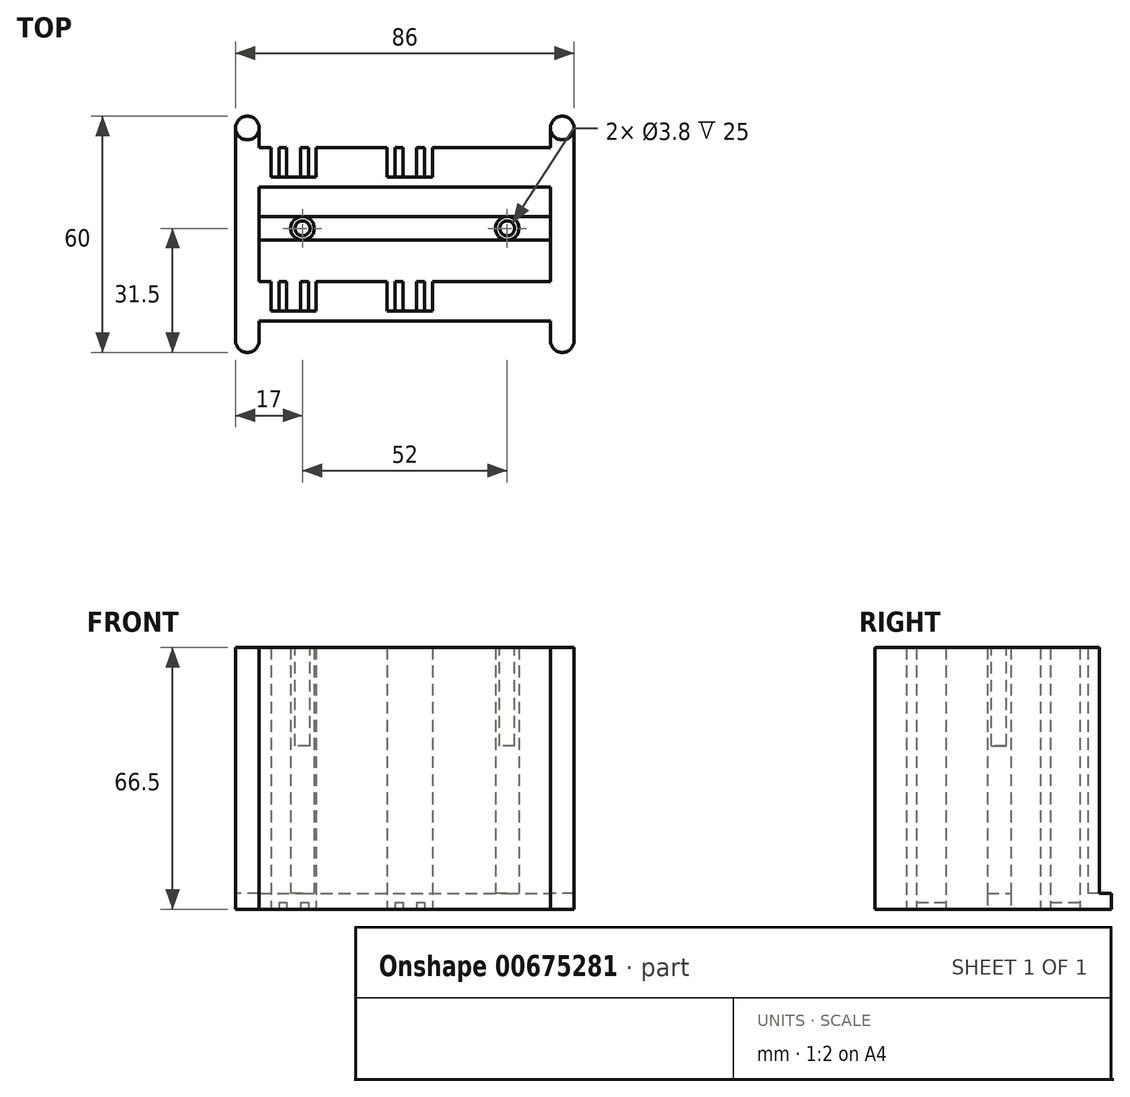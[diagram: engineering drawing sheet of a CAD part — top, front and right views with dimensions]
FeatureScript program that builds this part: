
annotation { "Feature Type Name" : "Feature", "Feature Type Description" : "" }
export const myFeature = defineFeature(function(context is Context, id is Id, definition is map)
    precondition{}
    {
        {
            var Q0;
            Q0=qCreatedBy(makeId("Top.planeOp"),FACE);
            var sketch = newSketch(context, id + "F0", { "sketchPlane" : qUnion([Q0])});
            skLineSegment(sketch, "E0", {"start": v(80, 0) * mm, "end": v(80, -39) * mm});
            skLineSegment(sketch, "E1", {"start": v(86, -39) * mm, "end": v(86, 15) * mm});
            skLineSegment(sketch, "E2", {"start": v(80, 15) * mm, "end": v(80, 10) * mm});
            skLineSegment(sketch, "E3", {"start": v(80, 10) * mm, "end": v(50, 10) * mm});
            skLineSegment(sketch, "E4", {"start": v(50, 10) * mm, "end": v(50, 2.5) * mm});
            skLineSegment(sketch, "E5", {"start": v(50, 2.5) * mm, "end": v(38.5, 2.5) * mm});
            skLineSegment(sketch, "E6", {"start": v(38.5, 2.5) * mm, "end": v(38.5, 10) * mm});
            skLineSegment(sketch, "E7", {"start": v(38.5, 10) * mm, "end": v(20.5, 10) * mm});
            skLineSegment(sketch, "E8", {"start": v(20.5, 10) * mm, "end": v(20.5, 2.5) * mm});
            skLineSegment(sketch, "E9", {"start": v(20.5, 2.5) * mm, "end": v(9, 2.5) * mm});
            skLineSegment(sketch, "E10", {"start": v(9, 2.5) * mm, "end": v(9, 10) * mm});
            skLineSegment(sketch, "E11", {"start": v(9, 10) * mm, "end": v(6, 10) * mm});
            skLineSegment(sketch, "E12", {"start": v(6, 10) * mm, "end": v(6, 15) * mm});
            skLineSegment(sketch, "E13", {"start": v(0, 15) * mm, "end": v(0, -39) * mm});
            skLineSegment(sketch, "E14", {"start": v(6, -39) * mm, "end": v(6, 0) * mm});
            skArc(sketch, "E15", {"start": v(0, 15) * mm, "mid": v(3, 18) * mm, "end": v(6, 15) * mm});
            skArc(sketch, "E16", {"start": v(6, -39) * mm, "mid": v(3, -42) * mm, "end": v(0, -39) * mm});
            skArc(sketch, "E17", {"start": v(86, -39) * mm, "mid": v(83, -42) * mm, "end": v(80, -39) * mm});
            skArc(sketch, "E18", {"start": v(80, 15) * mm, "mid": v(83, 18) * mm, "end": v(86, 15) * mm});
            skLineSegment(sketch, "E19", {"start": v(6, 0) * mm, "end": v(80, 0) * mm});
            skLineSegment(sketch, "E20.0.1.0", {"start": v(9, -24) * mm, "end": v(6, -24) * mm});
            skLineSegment(sketch, "E20.0.1.1", {"start": v(9, -31.5) * mm, "end": v(9, -24) * mm});
            skLineSegment(sketch, "E20.0.1.2", {"start": v(20.5, -31.5) * mm, "end": v(9, -31.5) * mm});
            skLineSegment(sketch, "E20.0.1.3", {"start": v(6, -34) * mm, "end": v(80, -34) * mm});
            skLineSegment(sketch, "E20.0.1.4", {"start": v(38.5, -24) * mm, "end": v(20.5, -24) * mm});
            skLineSegment(sketch, "E20.0.1.5", {"start": v(20.5, -24) * mm, "end": v(20.5, -31.5) * mm});
            skLineSegment(sketch, "E20.0.1.6", {"start": v(38.5, -31.5) * mm, "end": v(38.5, -24) * mm});
            skLineSegment(sketch, "E20.0.1.7", {"start": v(50, -31.5) * mm, "end": v(38.5, -31.5) * mm});
            skLineSegment(sketch, "E20.0.1.8", {"start": v(50, -24) * mm, "end": v(50, -31.5) * mm});
            skLineSegment(sketch, "E20.0.1.9", {"start": v(80, -24) * mm, "end": v(50, -24) * mm});
            skLineSegment(sketch, "E20.direction1", {"start": v(6, 10) * mm, "end": v(25.1, 10) * mm, "construction": true});
            skLineSegment(sketch, "E20.direction2", {"start": v(6, 10) * mm, "end": v(6, -24) * mm, "construction": true});
            skSolve(sketch);
        }
        {
            var Q0;
            Q0=makeQuery(id+"F0.imprint","IMPRINT",FACE,{"disambiguationData":[TD([[makeQuery(id+"F0.imprint","IMPRINT",EDGE,{"derivedFrom":sQuery(id+"F0.wireOp",EDGE,"E0")}),1.0]])]});
            var Q1;
            {var subQ3=sQuery(id+"F0.wireOp",EDGE,"E20.0.1.0");Q1=makeQuery(id+"F0.imprint","IMPRINT",FACE,{"disambiguationData":[TD([[makeQuery(id+"F0.imprint","IMPRINT",EDGE,{"derivedFrom":subQ3}),1.0]])]});}
            extrude(context, id + "F1", {"entities" : qUnion([Q0, Q1]), "depth" : 4 * mm, "offsetDistance" : 25 * mm});
        }
        {
            var Q0;
            Q0=qCreatedBy(makeId("Top.planeOp"),FACE);
            var sketch = newSketch(context, id + "F2", { "sketchPlane" : qUnion([Q0])});
            skLineSegment(sketch, "E21.bottom", {"start": v(11, 2.5) * mm, "end": v(13, 2.5) * mm});
            skLineSegment(sketch, "E21.top", {"start": v(11, 10) * mm, "end": v(13, 10) * mm});
            skLineSegment(sketch, "E21.left", {"start": v(11, 2.5) * mm, "end": v(11, 10) * mm});
            skLineSegment(sketch, "E21.right", {"start": v(13, 2.5) * mm, "end": v(13, 10) * mm});
            skLineSegment(sketch, "E22.bottom", {"start": v(16.5, 2.5) * mm, "end": v(18.5, 2.5) * mm});
            skLineSegment(sketch, "E22.top", {"start": v(16.5, 10) * mm, "end": v(18.5, 10) * mm});
            skLineSegment(sketch, "E22.left", {"start": v(16.5, 2.5) * mm, "end": v(16.5, 10) * mm});
            skLineSegment(sketch, "E22.right", {"start": v(18.5, 2.5) * mm, "end": v(18.5, 10) * mm});
            skLineSegment(sketch, "E23.bottom", {"start": v(40.5, 2.5) * mm, "end": v(42.5, 2.5) * mm});
            skLineSegment(sketch, "E23.top", {"start": v(40.5, 10) * mm, "end": v(42.5, 10) * mm});
            skLineSegment(sketch, "E23.left", {"start": v(40.5, 2.5) * mm, "end": v(40.5, 10) * mm});
            skLineSegment(sketch, "E23.right", {"start": v(42.5, 2.5) * mm, "end": v(42.5, 10) * mm});
            skLineSegment(sketch, "E24.bottom", {"start": v(46, 2.5) * mm, "end": v(48, 2.5) * mm});
            skLineSegment(sketch, "E24.top", {"start": v(46, 10) * mm, "end": v(48, 10) * mm});
            skLineSegment(sketch, "E24.left", {"start": v(46, 2.5) * mm, "end": v(46, 10) * mm});
            skLineSegment(sketch, "E24.right", {"start": v(48, 2.5) * mm, "end": v(48, 10) * mm});
            skLineSegment(sketch, "E25.0.1.0", {"start": v(46, -31.5) * mm, "end": v(46, -24) * mm});
            skLineSegment(sketch, "E25.0.1.1", {"start": v(48, -31.5) * mm, "end": v(48, -24) * mm});
            skLineSegment(sketch, "E25.0.1.2", {"start": v(11, -31.5) * mm, "end": v(11, -24) * mm});
            skLineSegment(sketch, "E25.0.1.3", {"start": v(13, -31.5) * mm, "end": v(13, -24) * mm});
            skLineSegment(sketch, "E25.0.1.4", {"start": v(16.5, -31.5) * mm, "end": v(16.5, -24) * mm});
            skLineSegment(sketch, "E25.0.1.5", {"start": v(18.5, -31.5) * mm, "end": v(18.5, -24) * mm});
            skLineSegment(sketch, "E25.0.1.6", {"start": v(40.5, -31.5) * mm, "end": v(40.5, -24) * mm});
            skLineSegment(sketch, "E25.0.1.7", {"start": v(42.5, -31.5) * mm, "end": v(42.5, -24) * mm});
            skLineSegment(sketch, "E25.0.1.8", {"start": v(46, -24) * mm, "end": v(48, -24) * mm});
            skLineSegment(sketch, "E25.0.1.9", {"start": v(11, -31.5) * mm, "end": v(13, -31.5) * mm});
            skLineSegment(sketch, "E25.0.1.10", {"start": v(11, -24) * mm, "end": v(13, -24) * mm});
            skLineSegment(sketch, "E25.0.1.11", {"start": v(16.5, -31.5) * mm, "end": v(18.5, -31.5) * mm});
            skLineSegment(sketch, "E25.0.1.12", {"start": v(16.5, -24) * mm, "end": v(18.5, -24) * mm});
            skLineSegment(sketch, "E25.0.1.13", {"start": v(40.5, -31.5) * mm, "end": v(42.5, -31.5) * mm});
            skLineSegment(sketch, "E25.0.1.14", {"start": v(40.5, -24) * mm, "end": v(42.5, -24) * mm});
            skLineSegment(sketch, "E25.0.1.15", {"start": v(46, -31.5) * mm, "end": v(48, -31.5) * mm});
            skLineSegment(sketch, "E25.direction1", {"start": v(11, 2.5) * mm, "end": v(36, 2.5) * mm, "construction": true});
            skLineSegment(sketch, "E25.direction2", {"start": v(11, 2.5) * mm, "end": v(11, -31.5) * mm, "construction": true});
            skSolve(sketch);
        }
        {
            var Q0;
            Q0=makeQuery(id+"F2.imprint","IMPRINT",FACE,{"disambiguationData":[TD([[makeQuery(id+"F2.imprint","IMPRINT",EDGE,{"derivedFrom":sQuery(id+"F2.wireOp",EDGE,"E21.bottom")}),1.0]])]});
            var Q1;
            Q1=makeQuery(id+"F2.imprint","IMPRINT",FACE,{"disambiguationData":[TD([[makeQuery(id+"F2.imprint","IMPRINT",EDGE,{"derivedFrom":sQuery(id+"F2.wireOp",EDGE,"E22.bottom")}),1.0]])]});
            var Q2;
            Q2=makeQuery(id+"F2.imprint","IMPRINT",FACE,{"disambiguationData":[TD([[makeQuery(id+"F2.imprint","IMPRINT",EDGE,{"derivedFrom":sQuery(id+"F2.wireOp",EDGE,"E23.bottom")}),1.0]])]});
            var Q3;
            Q3=makeQuery(id+"F2.imprint","IMPRINT",FACE,{"disambiguationData":[TD([[makeQuery(id+"F2.imprint","IMPRINT",EDGE,{"derivedFrom":sQuery(id+"F2.wireOp",EDGE,"E24.bottom")}),1.0]])]});
            var Q4;
            Q4=makeQuery(id+"F2.imprint","IMPRINT",FACE,{"disambiguationData":[TD([[makeQuery(id+"F2.imprint","IMPRINT",EDGE,{"derivedFrom":sQuery(id+"F2.wireOp",EDGE,"E25.0.1.2")}),-1.0]])]});
            var Q5;
            Q5=makeQuery(id+"F2.imprint","IMPRINT",FACE,{"disambiguationData":[TD([[makeQuery(id+"F2.imprint","IMPRINT",EDGE,{"derivedFrom":sQuery(id+"F2.wireOp",EDGE,"E25.0.1.4")}),-1.0]])]});
            var Q6;
            Q6=makeQuery(id+"F2.imprint","IMPRINT",FACE,{"disambiguationData":[TD([[makeQuery(id+"F2.imprint","IMPRINT",EDGE,{"derivedFrom":sQuery(id+"F2.wireOp",EDGE,"E25.0.1.6")}),-1.0]])]});
            var Q7;
            Q7=makeQuery(id+"F2.imprint","IMPRINT",FACE,{"disambiguationData":[TD([[makeQuery(id+"F2.imprint","IMPRINT",EDGE,{"derivedFrom":sQuery(id+"F2.wireOp",EDGE,"E25.0.1.0")}),-1.0]])]});
            extrude(context, id + "F3", {"entities" : qUnion([Q0, Q1, Q2, Q3, Q4, Q5, Q6, Q7]), "operationType" : NewBodyOperationType.ADD, "depth" : 1.7 * mm, "offsetDistance" : 25 * mm});
        }
        {
            var Q0;
            Q0=makeQuery(id+"F1.opExtrude","CAP_FACE",FACE,{"disambiguationData":[OSD([sQuery(id+"F0.wireOp",EDGE,"E0"),sQuery(id+"F0.wireOp",EDGE,"E1"),sQuery(id+"F0.wireOp",EDGE,"E2"),sQuery(id+"F0.wireOp",EDGE,"E3"),sQuery(id+"F0.wireOp",EDGE,"E4"),sQuery(id+"F0.wireOp",EDGE,"E5"),sQuery(id+"F0.wireOp",EDGE,"E6"),sQuery(id+"F0.wireOp",EDGE,"E7"),sQuery(id+"F0.wireOp",EDGE,"E8"),sQuery(id+"F0.wireOp",EDGE,"E9"),sQuery(id+"F0.wireOp",EDGE,"E10"),sQuery(id+"F0.wireOp",EDGE,"E11"),sQuery(id+"F0.wireOp",EDGE,"E12"),sQuery(id+"F0.wireOp",EDGE,"E13"),sQuery(id+"F0.wireOp",EDGE,"E14"),sQuery(id+"F0.wireOp",EDGE,"E15"),sQuery(id+"F0.wireOp",EDGE,"E16"),sQuery(id+"F0.wireOp",EDGE,"E17"),sQuery(id+"F0.wireOp",EDGE,"E18"),sQuery(id+"F0.wireOp",EDGE,"E19")])],"isStart":false});
            var sketch = newSketch(context, id + "F4", { "sketchPlane" : qUnion([Q0])});
            skCircle(sketch, "E26", {"center": v(3, 15) * mm, "radius": 3 * mm});
            skCircle(sketch, "E27", {"center": v(83, 15) * mm, "radius": 3 * mm});
            skCircle(sketch, "E28", {"center": v(83, -39) * mm, "radius": 3 * mm});
            skCircle(sketch, "E29", {"center": v(3, -39) * mm, "radius": 3 * mm});
            skCircle(sketch, "E30", {"center": v(17, -10.5) * mm, "radius": 3 * mm});
            skCircle(sketch, "E31", {"center": v(69, -10.5) * mm, "radius": 3 * mm});
            skSolve(sketch);
        }
        {
            var Q0;
            {var subQ0=sQuery(id+"F4.wireOp",EDGE,"E26");Q0=makeQuery(id+"F4.imprint","IMPRINT",FACE,{"disambiguationData":[TD([[makeQuery(id+"F4.imprint","IMPRINT",EDGE,{"disambiguationData":[OD(0.0)],"derivedFrom":subQ0}),-1.0]])]});}
            var Q1;
            {var subQ0=sQuery(id+"F4.wireOp",EDGE,"E29");Q1=makeQuery(id+"F4.imprint","IMPRINT",FACE,{"disambiguationData":[TD([[makeQuery(id+"F4.imprint","IMPRINT",EDGE,{"disambiguationData":[OD(0.0)],"derivedFrom":subQ0}),1.0]])]});}
            var Q2;
            {var subQ0=sQuery(id+"F4.wireOp",EDGE,"E27");Q2=makeQuery(id+"F4.imprint","IMPRINT",FACE,{"disambiguationData":[TD([[makeQuery(id+"F4.imprint","IMPRINT",EDGE,{"disambiguationData":[OD(0.0)],"derivedFrom":subQ0}),-1.0]])]});}
            var Q3;
            {var subQ0=sQuery(id+"F4.wireOp",EDGE,"E28");Q3=makeQuery(id+"F4.imprint","IMPRINT",FACE,{"disambiguationData":[TD([[makeQuery(id+"F4.imprint","IMPRINT",EDGE,{"disambiguationData":[OD(0.0)],"derivedFrom":subQ0}),1.0]])]});}
            var Q4;
            Q4=makeQuery(id+"F4.imprint","IMPRINT",FACE,{"disambiguationData":[TD([[makeQuery(id+"F4.imprint","IMPRINT",EDGE,{"derivedFrom":sQuery(id+"F4.wireOp",EDGE,"E30")}),1.0]])]});
            var Q5;
            Q5=makeQuery(id+"F4.imprint","IMPRINT",FACE,{"disambiguationData":[TD([[makeQuery(id+"F4.imprint","IMPRINT",EDGE,{"derivedFrom":sQuery(id+"F4.wireOp",EDGE,"E31")}),1.0]])]});
            extrude(context, id + "F5", {"entities" : qUnion([Q0, Q1, Q2, Q3, Q4, Q5]), "operationType" : NewBodyOperationType.ADD, "depth" : (125 - 62.5) * mm, "offsetDistance" : 25 * mm});
        }
        {
            var Q0;
            Q0=makeQuery(id+"F3.boolean.opBoolean","MERGE",FACE,{"derivedFrom":[makeQuery(id+"F1.opExtrude","CAP_FACE",FACE,{"disambiguationData":[OSD([sQuery(id+"F0.wireOp",EDGE,"E0"),sQuery(id+"F0.wireOp",EDGE,"E1"),sQuery(id+"F0.wireOp",EDGE,"E2"),sQuery(id+"F0.wireOp",EDGE,"E3"),sQuery(id+"F0.wireOp",EDGE,"E4"),sQuery(id+"F0.wireOp",EDGE,"E5"),sQuery(id+"F0.wireOp",EDGE,"E6"),sQuery(id+"F0.wireOp",EDGE,"E7"),sQuery(id+"F0.wireOp",EDGE,"E8"),sQuery(id+"F0.wireOp",EDGE,"E9"),sQuery(id+"F0.wireOp",EDGE,"E10"),sQuery(id+"F0.wireOp",EDGE,"E11"),sQuery(id+"F0.wireOp",EDGE,"E12"),sQuery(id+"F0.wireOp",EDGE,"E13"),sQuery(id+"F0.wireOp",EDGE,"E14"),sQuery(id+"F0.wireOp",EDGE,"E15"),sQuery(id+"F0.wireOp",EDGE,"E16"),sQuery(id+"F0.wireOp",EDGE,"E17"),sQuery(id+"F0.wireOp",EDGE,"E18"),sQuery(id+"F0.wireOp",EDGE,"E19")])],"isStart":true}),makeQuery(id+"F3.opExtrude","CAP_FACE",FACE,{"disambiguationData":[OSD([sQuery(id+"F2.wireOp",EDGE,"E21.bottom"),sQuery(id+"F2.wireOp",EDGE,"E21.top"),sQuery(id+"F2.wireOp",EDGE,"E21.left"),sQuery(id+"F2.wireOp",EDGE,"E21.right")])],"isStart":true}),makeQuery(id+"F3.opExtrude","CAP_FACE",FACE,{"disambiguationData":[OSD([sQuery(id+"F2.wireOp",EDGE,"E22.bottom"),sQuery(id+"F2.wireOp",EDGE,"E22.top"),sQuery(id+"F2.wireOp",EDGE,"E22.left"),sQuery(id+"F2.wireOp",EDGE,"E22.right")])],"isStart":true}),makeQuery(id+"F3.opExtrude","CAP_FACE",FACE,{"disambiguationData":[OSD([sQuery(id+"F2.wireOp",EDGE,"E23.bottom"),sQuery(id+"F2.wireOp",EDGE,"E23.top"),sQuery(id+"F2.wireOp",EDGE,"E23.left"),sQuery(id+"F2.wireOp",EDGE,"E23.right")])],"isStart":true}),makeQuery(id+"F3.opExtrude","CAP_FACE",FACE,{"disambiguationData":[OSD([sQuery(id+"F2.wireOp",EDGE,"E24.bottom"),sQuery(id+"F2.wireOp",EDGE,"E24.top"),sQuery(id+"F2.wireOp",EDGE,"E24.left"),sQuery(id+"F2.wireOp",EDGE,"E24.right")])],"isStart":true})]});
            var sketch = newSketch(context, id + "F6", { "sketchPlane" : qUnion([Q0])});
            skCircle(sketch, "E32", {"center": v(3, 39) * mm, "radius": 1 * mm});
            skCircle(sketch, "E33", {"center": v(83, 39) * mm, "radius": 1 * mm});
            skCircle(sketch, "E34", {"center": v(83, -15) * mm, "radius": 1 * mm});
            skCircle(sketch, "E35", {"center": v(3, -15) * mm, "radius": 1 * mm});
            skSolve(sketch);
        }
        {
            var Q0;
            Q0=makeQuery(id+"F6.imprint","IMPRINT",FACE,{"disambiguationData":[TD([[makeQuery(id+"F6.imprint","IMPRINT",EDGE,{"derivedFrom":sQuery(id+"F6.wireOp",EDGE,"E32")}),-1.0]])]});
            var sketch = newSketch(context, id + "F7", { "sketchPlane" : qUnion([Q0])});
            skLineSegment(sketch, "E36.bottom", {"start": v(6, 13.5) * mm, "end": v(80, 13.5) * mm});
            skLineSegment(sketch, "E36.top", {"start": v(6, 7.5) * mm, "end": v(80, 7.5) * mm});
            skLineSegment(sketch, "E36.left", {"start": v(6, 13.5) * mm, "end": v(6, 7.5) * mm});
            skLineSegment(sketch, "E36.right", {"start": v(80, 13.5) * mm, "end": v(80, 7.5) * mm});
            skSolve(sketch);
        }
        {
            var Q0;
            Q0=makeQuery(id+"F7.imprint","IMPRINT",FACE,{"disambiguationData":[TD([[makeQuery(id+"F7.imprint","IMPRINT",EDGE,{"derivedFrom":sQuery(id+"F7.wireOp",EDGE,"E36.bottom")}),-1.0]])]});
            extrude(context, id + "F8", {"entities" : qUnion([Q0]), "operationType" : NewBodyOperationType.ADD, "oppositeDirection" : true, "depth" : 4 * mm, "offsetDistance" : 25 * mm});
        }
        {
            var Q0;
            Q0=makeQuery(id+"F5.opExtrude","CAP_FACE",FACE,{"disambiguationData":[OSD([sQuery(id+"F4.wireOp",EDGE,"E30")])],"isStart":false});
            var sketch = newSketch(context, id + "F9", { "sketchPlane" : qUnion([Q0])});
            skCircle(sketch, "E37", {"center": v(17, -10.5) * mm, "radius": 1.9 * mm});
            skSolve(sketch);
        }
        {
            var Q0;
            Q0=makeQuery(id+"F5.opExtrude","CAP_FACE",FACE,{"disambiguationData":[OSD([sQuery(id+"F4.wireOp",EDGE,"E31")])],"isStart":false});
            var sketch = newSketch(context, id + "F10", { "sketchPlane" : qUnion([Q0])});
            skCircle(sketch, "E38", {"center": v(69, -10.5) * mm, "radius": 1.9 * mm});
            skSolve(sketch);
        }
        {
            var Q0;
            Q0=makeQuery(id+"F9.imprint","IMPRINT",FACE,{"disambiguationData":[TD([[makeQuery(id+"F9.imprint","IMPRINT",EDGE,{"derivedFrom":sQuery(id+"F9.wireOp",EDGE,"E37")}),1.0]])]});
            var Q1;
            Q1=makeQuery(id+"F10.imprint","IMPRINT",FACE,{"disambiguationData":[TD([[makeQuery(id+"F10.imprint","IMPRINT",EDGE,{"derivedFrom":sQuery(id+"F10.wireOp",EDGE,"E38")}),1.0]])]});
            extrude(context, id + "F11", {"entities" : qUnion([Q0, Q1]), "operationType" : NewBodyOperationType.REMOVE, "oppositeDirection" : true, "depth" : 25 * mm, "offsetDistance" : 25 * mm});
        }
    });
